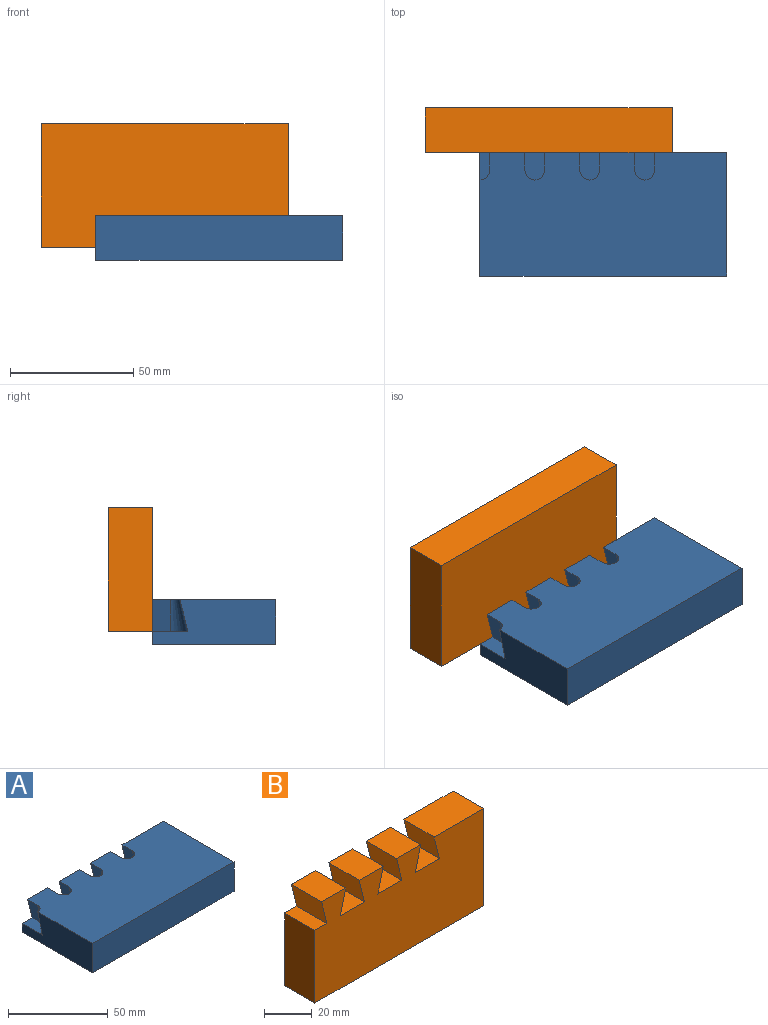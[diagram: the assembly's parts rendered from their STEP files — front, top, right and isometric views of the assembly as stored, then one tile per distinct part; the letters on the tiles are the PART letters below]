
ASSEMBLY  parts=2 mates=1
PART A: 21 faces, bbox 100x50x18 mm
  f0: plane 100x18mm, normal (0,1,0), area 1305.1mm2, adj f1,f3,f4,f5,f6,f7,f8,f10
  f1: plane 50x18mm, normal (-1,0,0), area 738.5mm2, adj f0,f2,f4,f5,f19,f20
  f2: plane 100x18mm, normal (0,-1,0), area 1800mm2, adj f1,f3,f4,f5
  f3: plane 50x18mm, normal (1,0,0), area 900mm2, adj f0,f2,f4,f5
  f4: plane 100x50mm, normal (0,0,-1), area 5000mm2, adj f0,f1,f2,f3
  f5: plane 100x50mm, normal (0,0,1), area 4713.4mm2, adj f0,f1,f2,f3,f6,f8,f9,f10
  f6: plane 12.7x7.15mm, normal (0.97,0,-0.24), area 93.6mm2, adj f0,f5,f7,f9
  f7: plane 14.3x14.3mm, normal (0,0,1), area 182.5mm2, adj f0,f6,f8,f9
  f8: plane 12.7x7.15mm, normal (-0.97,0,-0.24), area 93.6mm2, adj f0,f5,f7,f9
  f9: cone r=3.98mm half-angle=14deg, axis (0,0,-1), area 228.9mm2, adj f5,f6,f7,f8
  f10: plane 12.7x7.15mm, normal (0.97,0,-0.24), area 93.6mm2, adj f0,f5,f11,f13
  f11: plane 14.3x14.3mm, normal (0,0,1), area 182.5mm2, adj f0,f10,f12,f13
  f12: plane 12.7x7.15mm, normal (-0.97,0,-0.24), area 93.6mm2, adj f0,f5,f11,f13
  f13: cone r=3.98mm half-angle=14deg, axis (0,0,-1), area 228.9mm2, adj f5,f10,f11,f12
  f14: plane 12.7x7.15mm, normal (0.97,0,-0.24), area 93.6mm2, adj f0,f5,f15,f17
  f15: plane 14.3x14.3mm, normal (0,0,1), area 182.5mm2, adj f0,f14,f16,f17
  f16: plane 12.7x7.15mm, normal (-0.97,0,-0.24), area 93.6mm2, adj f0,f5,f15,f17
  f17: cone r=3.98mm half-angle=14deg, axis (0,0,-1), area 228.9mm2, adj f5,f14,f15,f16
  f18: plane 12.7x7.15mm, normal (-0.97,0,-0.24), area 93.6mm2, adj f0,f5,f19,f20
  f19: plane 14.3x7.15mm, normal (0,0,1), area 91.3mm2, adj f0,f1,f18,f20
  f20: cone r=3.98mm half-angle=14deg, axis (0,0,-1), area 114.5mm2, adj f1,f5,f18,f19
PART B: 20 faces, bbox 100x18x50 mm
  f0: plane 18x14.28mm, normal (0,0,1), area 257.1mm2, adj f5,f7,f15,f19
  f1: plane 18x14.28mm, normal (0,0,1), area 257.1mm2, adj f5,f7,f12,f17
  f2: plane 29.27x18mm, normal (0,0,1), area 526.8mm2, adj f5,f6,f7,f11
  f3: plane 18x14.28mm, normal (0,0,1), area 257.1mm2, adj f5,f7,f9,f14
  f4: plane 37.3x18mm, normal (-1,0,0), area 671.4mm2, adj f5,f7,f8,f18
  f5: plane 100x50mm, normal (0,-1,0), area 4505.1mm2, adj f0,f1,f2,f3,f4,f6,f8,f9
  f6: plane 50x18mm, normal (1,0,0), area 900mm2, adj f2,f5,f7,f8
  f7: plane 100x50mm, normal (0,1,0), area 4505.1mm2, adj f0,f1,f2,f3,f4,f6,f8,f9
  f8: plane 100x18mm, normal (0,0,-1), area 1800mm2, adj f4,f5,f6,f7
  f9: plane 18x12.7mm, normal (0.97,0,-0.24), area 235.6mm2, adj f3,f5,f7,f10
  f10: plane 18x14.3mm, normal (0,0,1), area 257.4mm2, adj f5,f7,f9,f11
  f11: plane 18x12.7mm, normal (-0.97,0,-0.24), area 235.6mm2, adj f2,f5,f7,f10
  f12: plane 18x12.7mm, normal (0.97,0,-0.24), area 235.6mm2, adj f1,f5,f7,f13
  f13: plane 18x14.3mm, normal (0,0,1), area 257.4mm2, adj f5,f7,f12,f14
  f14: plane 18x12.7mm, normal (-0.97,0,-0.24), area 235.6mm2, adj f3,f5,f7,f13
  f15: plane 18x12.7mm, normal (0.97,0,-0.24), area 235.6mm2, adj f0,f5,f7,f16
  f16: plane 18x14.3mm, normal (0,0,1), area 257.4mm2, adj f5,f7,f15,f17
  f17: plane 18x12.7mm, normal (-0.97,0,-0.24), area 235.6mm2, adj f1,f5,f7,f16
  f18: plane 18x7.15mm, normal (0,0,1), area 128.7mm2, adj f4,f5,f7,f19
  f19: plane 18x12.7mm, normal (-0.97,0,-0.24), area 235.6mm2, adj f0,f5,f7,f18
PLACE A t=(-35.17,-8.87,-7.22)mm
PLACE B rot(axis=(0,-1,0),180deg) t=(42.72,-8.87,-19.92)mm
MATE fastened A.f0 <-> B.f5  axis (0,1,0) through (-28.02,-1.72,-19.92)mm
